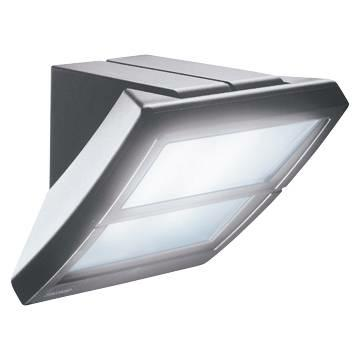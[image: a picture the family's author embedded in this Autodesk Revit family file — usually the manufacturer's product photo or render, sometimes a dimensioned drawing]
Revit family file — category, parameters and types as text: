
# Revit family: Lighting-ArredoUrbano-GEWISS-EXTRO-APPARECCHI_POLIFUNZIONALI
name_source: partatom
category: Apparecchi per illuminazione
units: mm (PartAtom-declared; Revit-internal decimal feet)

## family parameters
Basato su piano di lavoro = Sì
Condiviso = No
Numero OmniClass = 23.80.70.14.21
Punto di calcolo locali = Sì
Quota connettore circolare = Usa diametro
Sempre verticale = Sì
Sorgente d'illuminazione = No
Taglio con vuoti quando caricato = No
Tipo di parte = Normale
Titolo OmniClass = Street and Roadway Lighting

## types (4) — shared parameters
Altezza da terra = 915 mm
Applicazione = Interno / Esterno
Carico apparente = 0 VA
Catalogo = LIGHTING
Catalogo Serie = EXTRO
Classe isolamento = I
Classificazione carico = Altro
Codice Electrocod = 2415
Colore = Grigio grafite
Cornice = GEWISS - Grigio Graffite
Distanza minima dall'oggetto illuminato = 1M
Glow Wire Test = 850°C
Grado di protezione = IP55
IDF = 8dd33221-3e67-4b86-82bd-b731a3886ad0
IDT = f88220e3-a173-4bf5-a06b-d8481c9e1565
Immagine tipo = GW82281S.jpg
Larghezza = 260 mm  [stored 0.853018 ft]
Materiale = Tecnopolimero
Numero poli = 1
Produttore = GEWISS S.p.A.
Prospetto di default = 1219 mm
Resistenza agli urti = IK09
SEO = Apparecchio polifunzionale
Scheda Tecnica = https://www.gewiss.com
Staffaggio = GEWISS - Grigio Graffite
Struttura = GEWISS - Grigio Graffite
Temperatura di utilizzo = -25 +25 °C
URL = https://www.gewiss.com
Versione file RFA = 20.11
Vetro led = GEWISS - Led - lm 1470 / Temp_4000 K (Ra 80)
Voltaggio = 0 V

## per-type parameters (varying)
- GW82281S - EXTRO C/L 70W SE 230V-50HZ G.GRAF.: Attacco lampada=E27; Classe di efficienza lampada fornita=A; Classe di efficienza lampade compatibili=A ÷ A+; Codice EAN=8011564210301; Descrizione=EXTRO CON LAMPADA 70W SE 230V-50HZ GRIGIO; Lampada in dotazione=SE*; Lampada inclusa=Si; Modello=GW82281S; Peso (kg)=3,6; Peso (kg):=3,6; Potenza di sistema=13W; Potenza lampada=70W; Tensione=230 V - 50 Hz; Tipo alimentatore=Reattore elettromagnetico KCG; Tipo lampada=SE; Tipo versione=Standard
- GW82206 - EXTRO 100W E27 G.GRAF.: Attacco lampada=E27; Classe di efficienza lampade compatibili=D ÷ A+; Codice EAN=8011564210356; Descrizione=EXTRO PER LAMPADA 100W E27 GRIGIO; Lampada inclusa=No; Modello=GW82206; Peso (kg)=2,4; Peso (kg):=2,4; Potenza di sistema=13W; Potenza lampada=100W; Potenza lampada max=100W; Tipo lampada=E27; Tipo versione=Standard
- GW82286 - EXTRO 2X26-32W 220-240V 50-60HZ G.GRAF.: Attacco lampada=GX24q-3; Classe di efficienza lampade compatibili=A; Codice EAN=8011564210332; Descrizione=EXTRO PER 2 LAMPADE 26-32W 220-240V 50-60HZ GRIGIO; Lampada inclusa=No; Lampada:=FSM; Modello=GW82286; Numero lampade=2; Numero lampade:=2; Peso (kg)=2,5; Peso (kg):=2,5; Potenza di sistema=13W; Potenza lampada=26-32W; Tensione=220/240 V - 50/60 Hz; Tipo alimentatore=Reattore elettronico EVG; Tipo lampada=FSM; Tipo versione=Standard
- GW82246 - EXTRO 1X26-32W220-240V50-60HZ EM.P.1H GR: Accumulatori tipo=Nichel-Cadmio; Attacco lampada=GX24q-3; Autonomia=1H; Autonomia:=1H; Classe di efficienza lampade compatibili=A; Codice EAN=8011564202658; Descrizione=EXTRO PER LAMPADA FSM 26-32W 220-240V 50-60HZ EMERGENZA P 1H GRIGIO; Flusso luminoso in emergenza (lm)=135 / 90; Flusso luminoso in emergenza (lm):=135 / 90; Lampada:=FSM; Modello=GW82246; Peso (kg)=2,8; Peso (kg):=2,8; Potenza lampada=26-32W; Tensione=220/240 V - 50/60 Hz; Tipo alimentatore=Reattore elettronico EVG; Tipo lampada=FSM; Tipo versione=Emergenza

note: [stored X ft] marks values corroborated as IEEE doubles in the binary element streams (Revit-internal decimal feet)
